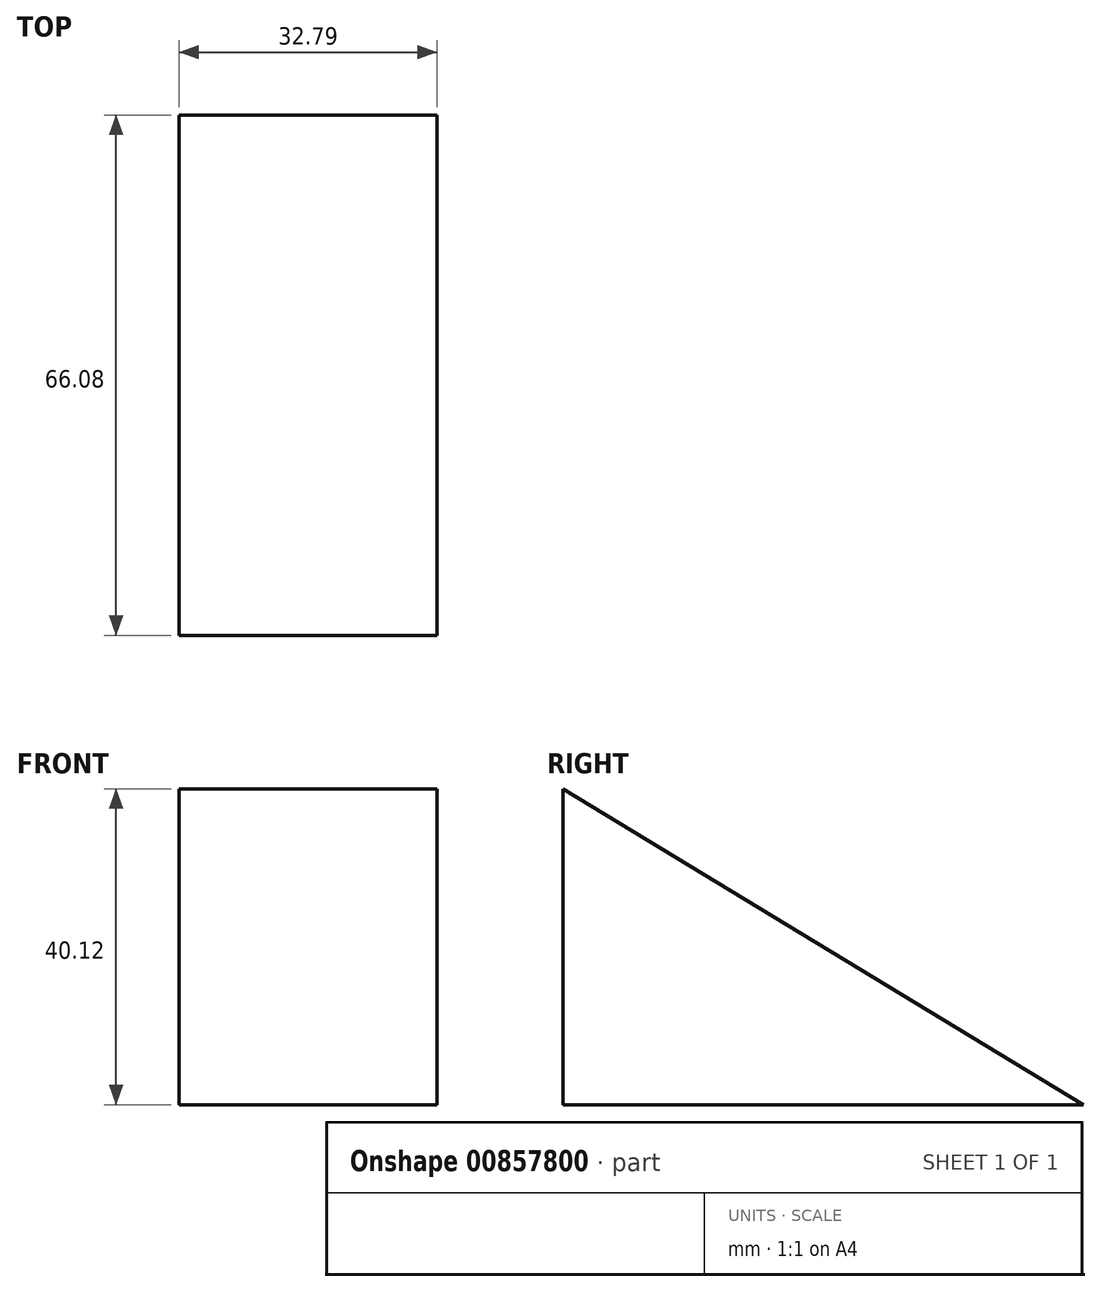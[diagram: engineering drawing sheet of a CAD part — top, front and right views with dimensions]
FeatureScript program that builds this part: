
annotation { "Feature Type Name" : "Feature", "Feature Type Description" : "" }
export const myFeature = defineFeature(function(context is Context, id is Id, definition is map)
    precondition{}
    {
        {
            var Q0;
            Q0=qCreatedBy(makeId("Right.planeOp"),FACE);
            var sketch = newSketch(context, id + "F0", { "sketchPlane" : qUnion([Q0])});
            skLineSegment(sketch, "E0", {"start": v(-69.8, 7.33) * mm, "end": v(-3.72, 7.33) * mm});
            skLineSegment(sketch, "E1", {"start": v(-69.8, 7.33) * mm, "end": v(-69.8, 47.45) * mm});
            skLineSegment(sketch, "E2", {"start": v(-69.8, 47.45) * mm, "end": v(-3.72, 7.33) * mm});
            skSolve(sketch);
        }
        {
            var Q0;
            Q0=makeQuery(id+"F0.imprint","IMPRINT",FACE,{"disambiguationData":[TD([[makeQuery(id+"F0.imprint","IMPRINT",EDGE,{"derivedFrom":sQuery(id+"F0.wireOp",EDGE,"E0")}),1.0]])]});
            extrude(context, id + "F1", {"entities" : qUnion([Q0]), "depth" : 32.8 * mm, "offsetDistance" : 25.4 * mm});
        }
    });
